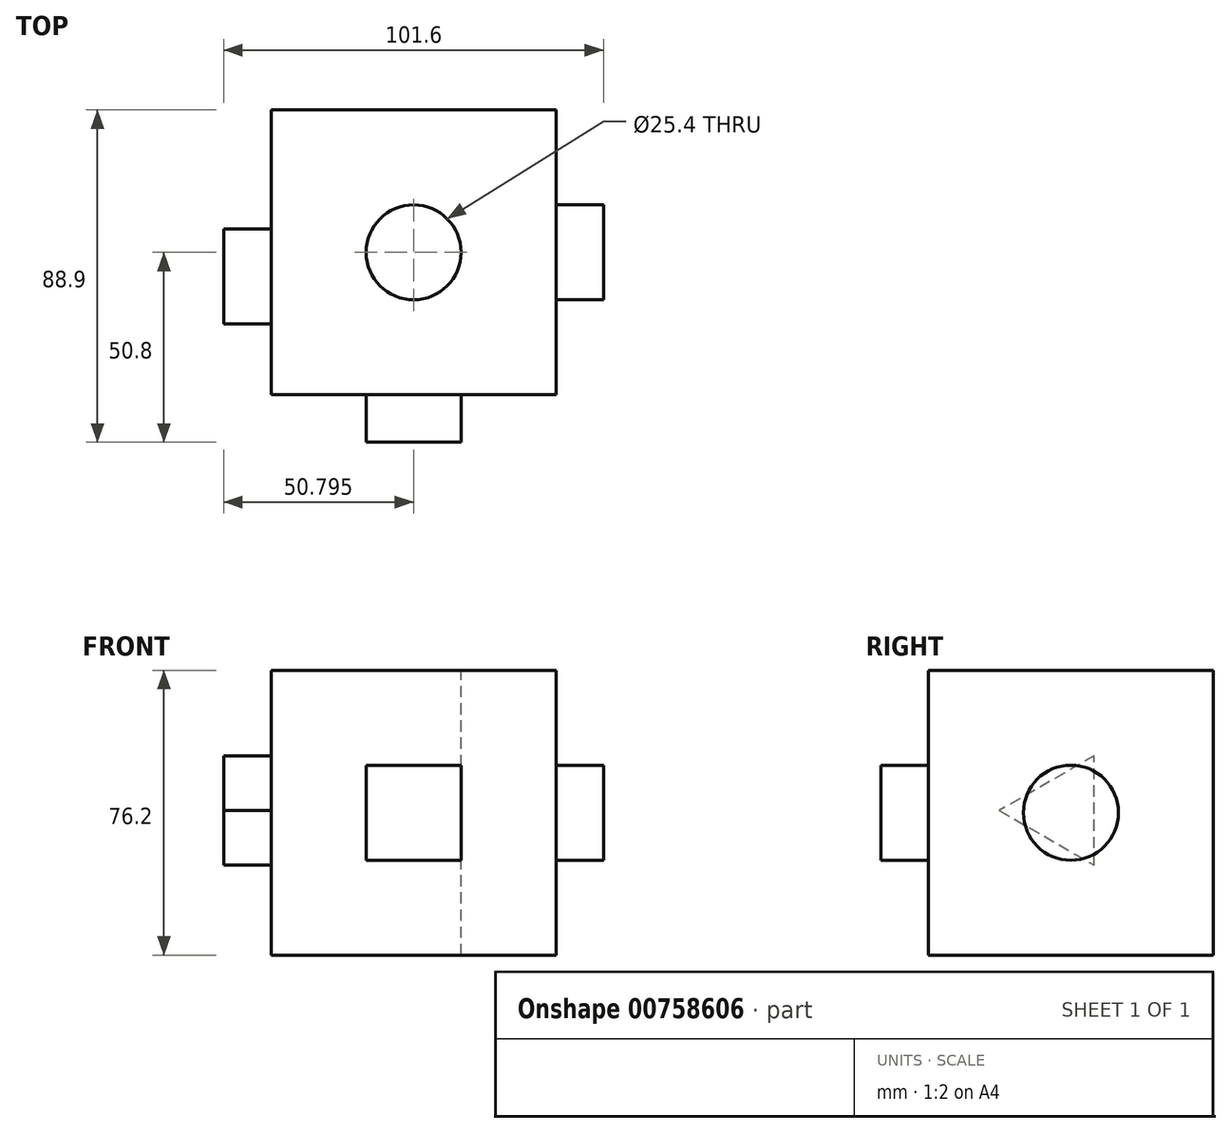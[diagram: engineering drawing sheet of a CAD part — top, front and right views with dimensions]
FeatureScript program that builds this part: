
annotation { "Feature Type Name" : "Feature", "Feature Type Description" : "" }
export const myFeature = defineFeature(function(context is Context, id is Id, definition is map)
    precondition{}
    {
        {
            var Q0;
            Q0=qCreatedBy(makeId("Front.planeOp"),FACE);
            var sketch = newSketch(context, id + "F0", { "sketchPlane" : qUnion([Q0])});
            skLineSegment(sketch, "E0.bottom", {"start": v(-39.2, 36.4) * mm, "end": v(37, 36.4) * mm});
            skLineSegment(sketch, "E0.top", {"start": v(-39.2, -39.8) * mm, "end": v(37, -39.8) * mm});
            skLineSegment(sketch, "E0.left", {"start": v(-39.2, 36.4) * mm, "end": v(-39.2, -39.8) * mm});
            skLineSegment(sketch, "E0.right", {"start": v(37, 36.4) * mm, "end": v(37, -39.8) * mm});
            skSolve(sketch);
        }
        {
            var Q0;
            Q0=makeQuery(id+"F0.imprint","IMPRINT",FACE,{"disambiguationData":[TD([[makeQuery(id+"F0.imprint","IMPRINT",EDGE,{"derivedFrom":sQuery(id+"F0.wireOp",EDGE,"E0.bottom")}),-1.0]])]});
            extrude(context, id + "F1", {"entities" : qUnion([Q0]), "depth" : 76.2 * mm, "offsetDistance" : 25.4 * mm});
        }
        {
            var Q0;
            Q0=makeQuery(id+"F1.opExtrude","CAP_FACE",FACE,{"disambiguationData":[OSD([sQuery(id+"F0.wireOp",EDGE,"E0.bottom"),sQuery(id+"F0.wireOp",EDGE,"E0.top"),sQuery(id+"F0.wireOp",EDGE,"E0.left"),sQuery(id+"F0.wireOp",EDGE,"E0.right")])],"isStart":false});
            var sketch = newSketch(context, id + "F2", { "sketchPlane" : qUnion([Q0])});
            skLineSegment(sketch, "E1.bottom", {"start": v(-13.8, 11) * mm, "end": v(11.6, 11) * mm});
            skLineSegment(sketch, "E1.top", {"start": v(-13.8, -14.4) * mm, "end": v(11.6, -14.4) * mm});
            skLineSegment(sketch, "E1.left", {"start": v(-13.8, 11) * mm, "end": v(-13.8, -14.4) * mm});
            skLineSegment(sketch, "E1.right", {"start": v(11.6, 11) * mm, "end": v(11.6, -14.4) * mm});
            skSolve(sketch);
        }
        {
            var Q0;
            Q0=makeQuery(id+"F2.imprint","IMPRINT",FACE,{"disambiguationData":[TD([[makeQuery(id+"F2.imprint","IMPRINT",EDGE,{"derivedFrom":sQuery(id+"F2.wireOp",EDGE,"E1.bottom")}),-1.0]])]});
            extrude(context, id + "F3", {"entities" : qUnion([Q0]), "operationType" : NewBodyOperationType.ADD, "depth" : 12.7 * mm, "offsetDistance" : 25.4 * mm});
        }
        {
            var Q0;
            Q0=makeQuery(id+"F1.opExtrude","SWEPT_FACE",FACE,{"disambiguationData":[OSD([sQuery(id+"F0.wireOp",EDGE,"E0.right")])]});
            var sketch = newSketch(context, id + "F4", { "sketchPlane" : qUnion([Q0])});
            skCircle(sketch, "E2", {"center": v(-38.1, -1.7) * mm, "radius": 12.7 * mm});
            skSolve(sketch);
        }
        {
            var Q0;
            Q0 = qSketchRegion(id + "F4", true);
            extrude(context, id + "F5", {"entities" : qUnion([Q0]), "operationType" : NewBodyOperationType.ADD, "depth" : 12.7 * mm, "offsetDistance" : 25.4 * mm});
        }
        {
            var Q0;
            Q0=makeQuery(id+"F1.opExtrude","SWEPT_FACE",FACE,{"disambiguationData":[OSD([sQuery(id+"F0.wireOp",EDGE,"E0.bottom")])]});
            var sketch = newSketch(context, id + "F6", { "sketchPlane" : qUnion([Q0])});
            skPoint(sketch, "E3", {"position": v(-1.1, -38.1) * mm});
            skSolve(sketch);
        }
        {
            var Q0;
            Q0=sQuery(id+"F6.wireOp",VERTEX,"E3");
            var Q1;
            Q1=makeQuery(id+"F1.opExtrude","SWEPT_BODY",BODY,{"disambiguationData":[OSD([sQuery(id+"F0.wireOp",EDGE,"E0.bottom"),sQuery(id+"F0.wireOp",EDGE,"E0.top"),sQuery(id+"F0.wireOp",EDGE,"E0.left"),sQuery(id+"F0.wireOp",EDGE,"E0.right")])]});
            hole(context, id + "F7", {"style" : HoleStyle.SIMPLE, "endStyle" : HoleEndStyle.THROUGH, "holeDiameter" : 25.4 * mm, "majorDiameter" : 6.35 * mm, "isTappedThrough" : true, "tappedDepth" : 12.7 * mm, "tapClearance" : 3, "locations" : qUnion([Q0]), "scope" : qUnion([Q1])});
        }
        {
            var Q0;
            Q0=makeQuery(id+"F1.opExtrude","SWEPT_FACE",FACE,{"disambiguationData":[OSD([sQuery(id+"F0.wireOp",EDGE,"E0.left")])]});
            var sketch = newSketch(context, id + "F8", { "sketchPlane" : qUnion([Q0])});
            skCircle(sketch, "E4.cCircle", {"center": v(40.3, -1.11) * mm, "radius": 8.47 * mm, "construction": true});
            skLineSegment(sketch, "E4.0", {"start": v(31.83, -15.78) * mm, "end": v(31.83, 13.55) * mm});
            skLineSegment(sketch, "E4.1", {"start": v(31.83, 13.55) * mm, "end": v(57.23, -1.11) * mm});
            skLineSegment(sketch, "E4.2", {"start": v(57.23, -1.11) * mm, "end": v(31.83, -15.78) * mm});
            skPoint(sketch, "E4.0.midPoint", {"position": v(31.83, -1.11) * mm});
            skSolve(sketch);
        }
        {
            var Q0;
            Q0=makeQuery(id+"F8.imprint","IMPRINT",FACE,{"disambiguationData":[TD([[makeQuery(id+"F8.imprint","IMPRINT",EDGE,{"derivedFrom":sQuery(id+"F8.wireOp",EDGE,"E4.0")}),-1.0]])]});
            extrude(context, id + "F9", {"entities" : qUnion([Q0]), "operationType" : NewBodyOperationType.ADD, "depth" : 12.7 * mm, "offsetDistance" : 25.4 * mm});
        }
    });
